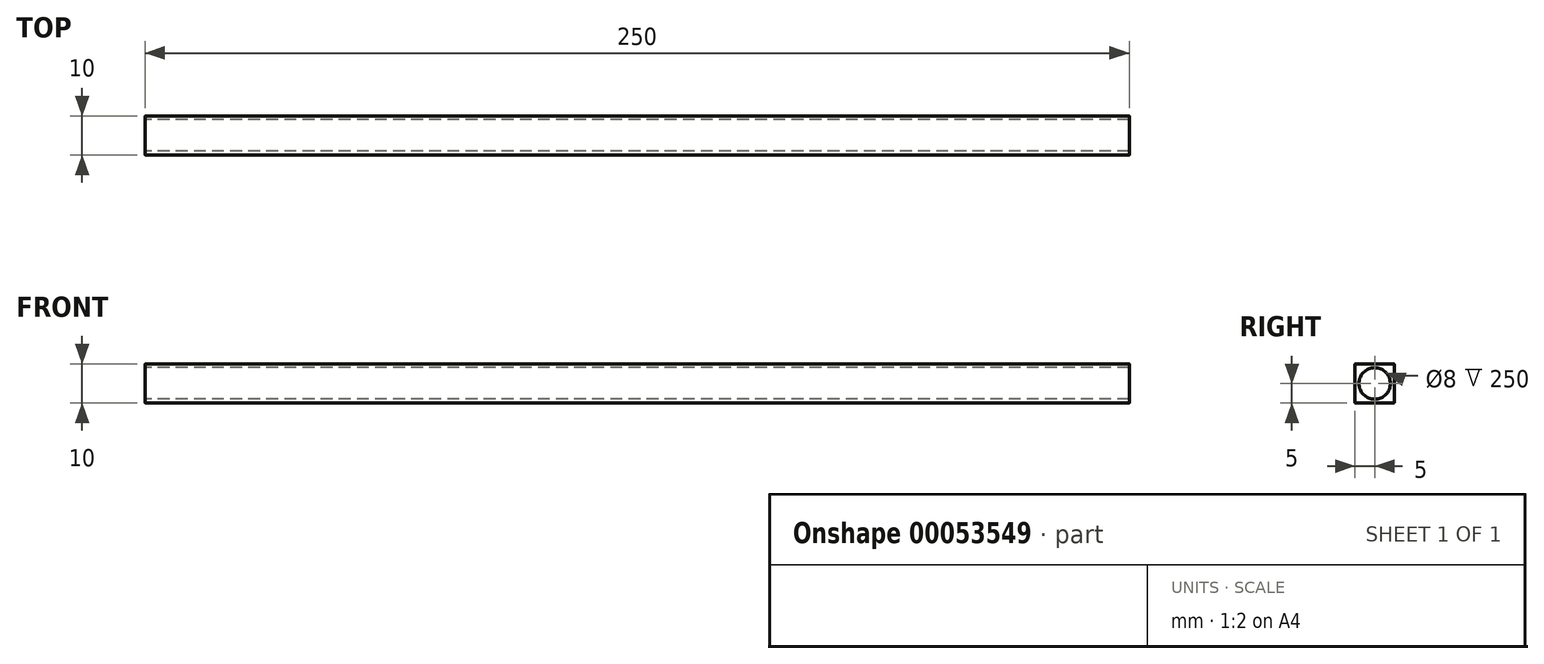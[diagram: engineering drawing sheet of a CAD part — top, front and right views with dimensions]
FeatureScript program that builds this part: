
annotation { "Feature Type Name" : "Feature", "Feature Type Description" : "" }
export const myFeature = defineFeature(function(context is Context, id is Id, definition is map)
    precondition{}
    {
        {
            var Q0;
            Q0=qCreatedBy(makeId("Right.planeOp"),FACE);
            var sketch = newSketch(context, id + "F0", { "sketchPlane" : qUnion([Q0])});
            skLineSegment(sketch, "E0.rect.bottom", {"start": v(5, -5) * mm, "end": v(-5, -5) * mm});
            skLineSegment(sketch, "E0.rect.top", {"start": v(5, 5) * mm, "end": v(-5, 5) * mm});
            skLineSegment(sketch, "E0.rect.left", {"start": v(5, -5) * mm, "end": v(5, 5) * mm});
            skLineSegment(sketch, "E0.rect.right", {"start": v(-5, -5) * mm, "end": v(-5, 5) * mm});
            skPoint(sketch, "E0.rect.middle", {"position": v(0, 0) * mm});
            skCircle(sketch, "E1", {"center": v(0, 0) * mm, "radius": 4 * mm});
            skSolve(sketch);
        }
        {
            var Q0;
            Q0=makeQuery(id+"F0.imprint","IMPRINT",FACE,{"disambiguationData":[TD([[makeQuery(id+"F0.imprint","IMPRINT",EDGE,{"derivedFrom":sQuery(id+"F0.wireOp",EDGE,"E0.rect.bottom")}),-1.0]])]});
            extrude(context, id + "F1", {"entities" : qUnion([Q0]), "depth" : 250 * mm});
        }
        {
            var Q0;
            Q0=makeQuery(id+"F1.opExtrude","SWEPT_EDGE",EDGE,{"disambiguationData":[OSD([sQuery(id+"F0.wireOp",EDGE,"E0.rect.top"),sQuery(id+"F0.wireOp",EDGE,"E0.rect.left")])]});
            var Q1;
            Q1=makeQuery(id+"F1.opExtrude","SWEPT_EDGE",EDGE,{"disambiguationData":[OSD([sQuery(id+"F0.wireOp",EDGE,"E0.rect.bottom"),sQuery(id+"F0.wireOp",EDGE,"E0.rect.left")])]});
            var Q2;
            Q2=makeQuery(id+"F1.opExtrude","SWEPT_EDGE",EDGE,{"disambiguationData":[OSD([sQuery(id+"F0.wireOp",EDGE,"E0.rect.top"),sQuery(id+"F0.wireOp",EDGE,"E0.rect.right")])]});
            var Q3;
            Q3=makeQuery(id+"F1.opExtrude","SWEPT_EDGE",EDGE,{"disambiguationData":[OSD([sQuery(id+"F0.wireOp",EDGE,"E0.rect.bottom"),sQuery(id+"F0.wireOp",EDGE,"E0.rect.right")])]});
            fillet(context, id + "F2", {"entities" : qUnion([Q0, Q1, Q2, Q3]), "radius" : .2 * mm, "tangentPropagation" : true, "allowEdgeOverflow" : false});
        }
    });
